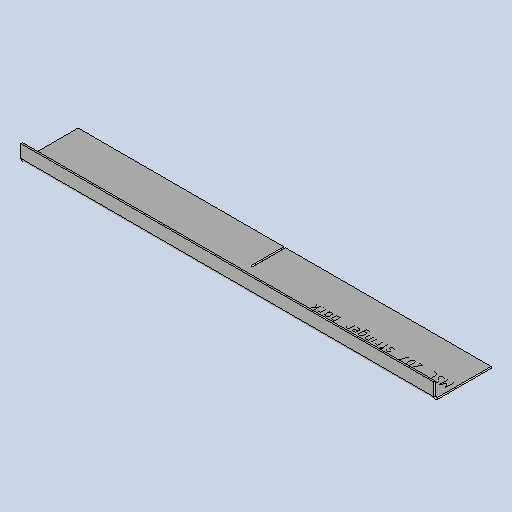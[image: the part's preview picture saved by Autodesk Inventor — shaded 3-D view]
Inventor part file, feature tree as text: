
AUTODESK INVENTOR PART (.ipt)
format: ipt  version: 2025 (Build 290162010, 162A)  size: 259,072 bytes
history: native  units: mm
features: other x5, sheet_metal_op x4, sketch x4, extrude x1
ambient origin geometry x8: Origin, YZ Plane, XZ Plane, XY Plane, X Axis, Y Axis, Z Axis, Center Point
bodies: Solid1 (feature_tree)
feature tree (14):
  sheet_metal_op  "Face1"
  sheet_metal_op  "Flange1"
  extrude  "Extrusion1"  Depth=68.0mm
  other  "Mark2"
  other  "A-Side Definition"
  sketch  "Sketch1"  dims[d0=980.0mm d1=68.0mm]
  other  "Plate1"
  sketch  "Sketch2"  dims[d2=2.0mm]
  other  "Plate2"
  sheet_metal_op  "Bend1"
  sheet_metal_op  "Corner1"
  sketch  "Sketch5"  dims[d3=2.0mm]
  sketch  "Sketch9"  dims[d4=1.0mm d5=4.0mm d6=2.75mm d7=20.0mm d8=90.0deg d9=2.75mm d10=8.0mm d11=2.0mm d12=2.75mm d15=0.0mm d16=0.0mm d40=200.0mm d41=12.0mm d45=70.0mm d48=2.1mm d49=490.0mm d51=29.0mm d52=39.0mm]
  other  "Definition1"
